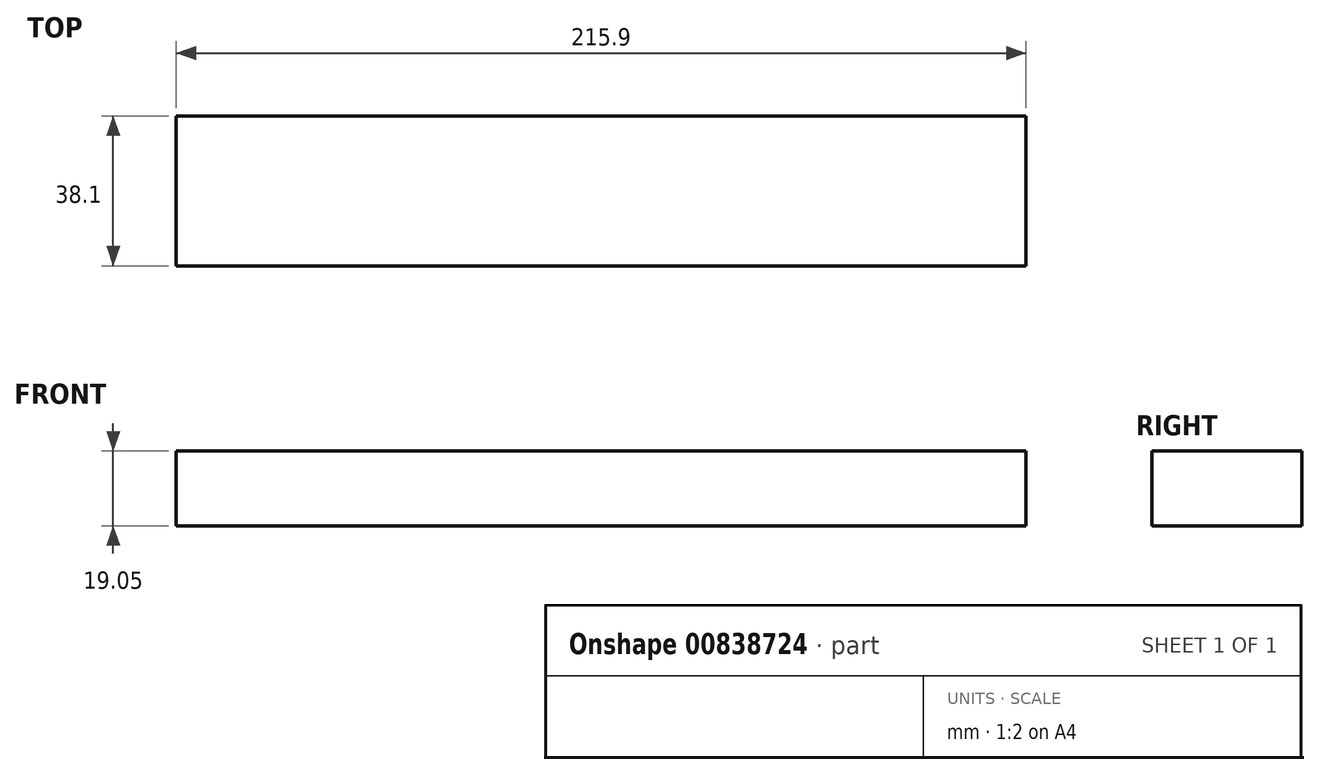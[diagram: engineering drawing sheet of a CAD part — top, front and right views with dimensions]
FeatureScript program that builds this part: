
annotation { "Feature Type Name" : "Feature", "Feature Type Description" : "" }
export const myFeature = defineFeature(function(context is Context, id is Id, definition is map)
    precondition{}
    {
        {
            var Q0;
            Q0=qCreatedBy(makeId("Front.planeOp"),FACE);
            var sketch = newSketch(context, id + "F0", { "sketchPlane" : qUnion([Q0])});
            skLineSegment(sketch, "E0.bottom", {"start": v(0, 0) * mm, "end": v(-215.9, 0) * mm});
            skLineSegment(sketch, "E0.top", {"start": v(0, 19.05) * mm, "end": v(-215.9, 19.05) * mm});
            skLineSegment(sketch, "E0.left", {"start": v(0, 0) * mm, "end": v(0, 19.05) * mm});
            skLineSegment(sketch, "E0.right", {"start": v(-215.9, 0) * mm, "end": v(-215.9, 19.05) * mm});
            skSolve(sketch);
        }
        {
            var Q0;
            Q0=qSketchRegion(id+"F0",true);
            extrude(context, id + "F1", {"entities" : qUnion([Q0]), "depth" : 38.1 * mm, "offsetDistance" : 25.4 * mm});
        }
    });
